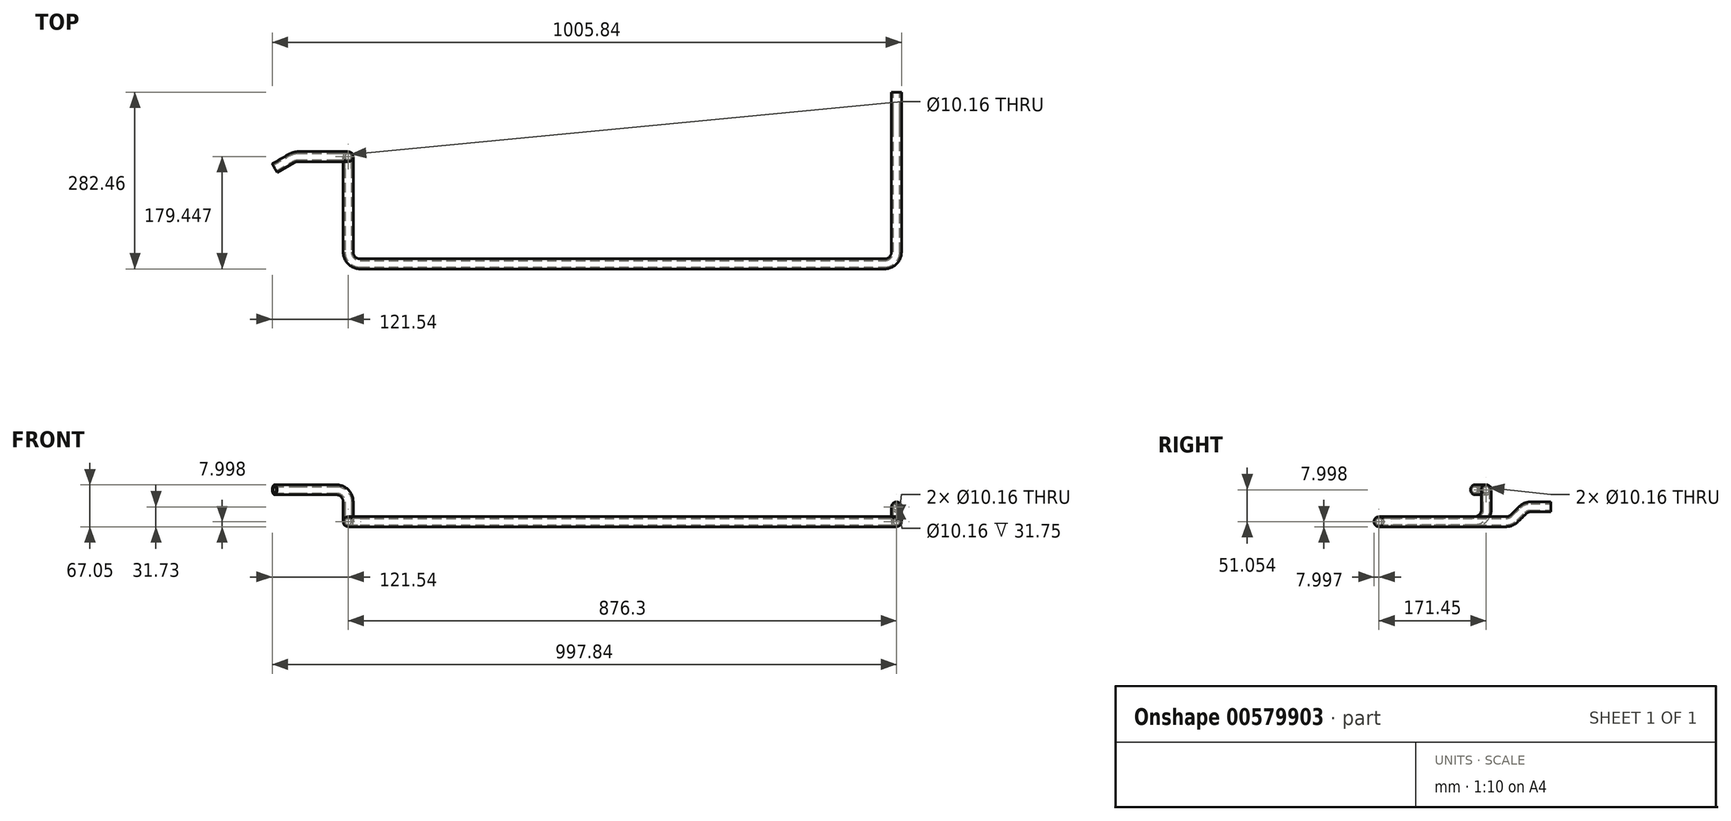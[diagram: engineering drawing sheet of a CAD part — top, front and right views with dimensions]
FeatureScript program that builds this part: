
annotation { "Feature Type Name" : "Feature", "Feature Type Description" : "" }
export const myFeature = defineFeature(function(context is Context, id is Id, definition is map)
    precondition{}
    {
        {
            var Q0;
            Q0=qCreatedBy(makeId("Front.planeOp"),FACE);
            var sketch = newSketch(context, id + "F0", { "sketchPlane" : qUnion([Q0])});
            skCircle(sketch, "E0", {"center": v(0, 0) * mm, "radius": 8 * mm});
            skCircle(sketch, "E1", {"center": v(0, 0) * mm, "radius": 5.08 * mm});
            skSolve(sketch);
        }
        {
            var Q0;
            Q0=qSketchRegion(id+"F0",true);
            extrude(context, id + "F1", {"entities" : qUnion([Q0]), "depth" : 31.75 * mm, "offsetDistance" : 25.4 * mm});
        }
        {
            var Q0;
            Q0=makeQuery(id+"F1.opExtrude","CAP_FACE",FACE,{"disambiguationData":[OSD([sQuery(id+"F0.wireOp",EDGE,"E0"),sQuery(id+"F0.wireOp",EDGE,"E1")])],"isStart":false});
            var sketch = newSketch(context, id + "F2", { "sketchPlane" : qUnion([Q0])});
            skCircle(sketch, "E2", {"center": v(0, 0) * mm, "radius": 5.08 * mm});
            skCircle(sketch, "E3", {"center": v(0, 0) * mm, "radius": 8 * mm});
            skLineSegment(sketch, "E4", {"start": v(-12.88, -19.05) * mm, "end": v(12.35, -19.05) * mm});
            skSolve(sketch);
        }
        {
            var Q0;
            Q0 = qSketchRegion(id + "F2", true);
            var Q1;
            Q1=sQuery(id+"F2.wireOp",EDGE,"E4");
            revolve(context, id + "F3", {"operationType" : NewBodyOperationType.ADD, "entities" : qUnion([Q0]), "axis" : qUnion([Q1]), "revolveType" : RevolveType.ONE_DIRECTION, "angle" : 45 * degree});
        }
        {
            var Q0;
            Q0=makeQuery(id+"F3.opRevolve","CAP_FACE",FACE,{"disambiguationData":[OSD([sQuery(id+"F2.wireOp",EDGE,"E2"),sQuery(id+"F2.wireOp",EDGE,"E3")])],"isStart":false});
            var sketch = newSketch(context, id + "F4", { "sketchPlane" : qUnion([Q0])});
            skCircle(sketch, "E5", {"center": v(0, 28.03) * mm, "radius": 5.08 * mm});
            skCircle(sketch, "E6", {"center": v(0, 28.03) * mm, "radius": 8 * mm});
            skSolve(sketch);
        }
        {
            var Q0;
            Q0 = qSketchRegion(id + "F4", true);
            extrude(context, id + "F5", {"entities" : qUnion([Q0]), "operationType" : NewBodyOperationType.ADD, "depth" : 17.78 * mm, "offsetDistance" : 25.4 * mm});
        }
        {
            var Q0;
            Q0=makeQuery(id+"F5.opExtrude","CAP_FACE",FACE,{"disambiguationData":[OSD([sQuery(id+"F4.wireOp",EDGE,"E5"),sQuery(id+"F4.wireOp",EDGE,"E6")])],"isStart":false});
            var sketch = newSketch(context, id + "F6", { "sketchPlane" : qUnion([Q0])});
            skCircle(sketch, "E7", {"center": v(0, 28.03) * mm, "radius": 5.08 * mm});
            skCircle(sketch, "E8", {"center": v(0, 28.03) * mm, "radius": 8 * mm});
            skLineSegment(sketch, "E9", {"start": v(-8.48, 47.08) * mm, "end": v(8.76, 47.08) * mm});
            skSolve(sketch);
        }
        {
            var Q0;
            Q0 = qSketchRegion(id + "F6", true);
            var Q1;
            Q1=sQuery(id+"F6.wireOp",EDGE,"E9");
            revolve(context, id + "F7", {"operationType" : NewBodyOperationType.ADD, "entities" : qUnion([Q0]), "axis" : qUnion([Q1]), "revolveType" : RevolveType.ONE_DIRECTION, "oppositeDirection" : true, "angle" : 45 * degree});
        }
        {
            var Q0;
            Q0=makeQuery(id+"F7.opRevolve","CAP_FACE",FACE,{"disambiguationData":[OSD([sQuery(id+"F6.wireOp",EDGE,"E7"),sQuery(id+"F6.wireOp",EDGE,"E8")])],"isStart":false});
            var sketch = newSketch(context, id + "F8", { "sketchPlane" : qUnion([Q0])});
            skCircle(sketch, "E10", {"center": v(0, -23.73) * mm, "radius": 5.08 * mm});
            skCircle(sketch, "E11", {"center": v(0, -23.73) * mm, "radius": 8 * mm});
            skSolve(sketch);
        }
        {
            var Q0;
            Q0 = qSketchRegion(id + "F8", true);
            extrude(context, id + "F9", {"entities" : qUnion([Q0]), "operationType" : NewBodyOperationType.ADD, "depth" : 184.15 * mm, "offsetDistance" : 25.4 * mm});
        }
        {
            var Q0;
            Q0=makeQuery(id+"F9.opExtrude","CAP_FACE",FACE,{"disambiguationData":[OSD([sQuery(id+"F8.wireOp",EDGE,"E10"),sQuery(id+"F8.wireOp",EDGE,"E11")])],"isStart":false});
            var sketch = newSketch(context, id + "F10", { "sketchPlane" : qUnion([Q0])});
            skCircle(sketch, "E12", {"center": v(0, -23.73) * mm, "radius": 5.08 * mm});
            skCircle(sketch, "E13", {"center": v(0, -23.73) * mm, "radius": 8 * mm});
            skLineSegment(sketch, "E14", {"start": v(-19.05, -18.56) * mm, "end": v(-19.05, -27.46) * mm});
            skSolve(sketch);
        }
        {
            var Q0;
            Q0 = qSketchRegion(id + "F10", true);
            var Q1;
            Q1=sQuery(id+"F10.wireOp",EDGE,"E14");
            revolve(context, id + "F11", {"operationType" : NewBodyOperationType.ADD, "entities" : qUnion([Q0]), "axis" : qUnion([Q1]), "revolveType" : RevolveType.ONE_DIRECTION, "angle" : 90 * degree});
        }
        {
            var Q0;
            Q0=makeQuery(id+"F11.opRevolve","CAP_FACE",FACE,{"disambiguationData":[OSD([sQuery(id+"F10.wireOp",EDGE,"E12"),sQuery(id+"F10.wireOp",EDGE,"E13")])],"isStart":false});
            var sketch = newSketch(context, id + "F12", { "sketchPlane" : qUnion([Q0])});
            skCircle(sketch, "E15", {"center": v(274.46, -23.73) * mm, "radius": 5.08 * mm});
            skCircle(sketch, "E16", {"center": v(274.46, -23.73) * mm, "radius": 8 * mm});
            skSolve(sketch);
        }
        {
            var Q0;
            Q0 = qSketchRegion(id + "F12", true);
            extrude(context, id + "F13", {"entities" : qUnion([Q0]), "operationType" : NewBodyOperationType.ADD, "depth" : 838.2 * mm, "offsetDistance" : 25.4 * mm});
        }
        {
            var Q0;
            Q0=makeQuery(id+"F13.opExtrude","CAP_FACE",FACE,{"disambiguationData":[OSD([sQuery(id+"F12.wireOp",EDGE,"E15"),sQuery(id+"F12.wireOp",EDGE,"E16")])],"isStart":false});
            var sketch = newSketch(context, id + "F14", { "sketchPlane" : qUnion([Q0])});
            skCircle(sketch, "E17", {"center": v(274.46, -23.73) * mm, "radius": 5.08 * mm});
            skCircle(sketch, "E18", {"center": v(274.46, -23.73) * mm, "radius": 8 * mm});
            skLineSegment(sketch, "E19", {"start": v(255.41, -17.25) * mm, "end": v(255.41, -29.27) * mm});
            skSolve(sketch);
        }
        {
            var Q0;
            Q0 = qSketchRegion(id + "F14", true);
            var Q1;
            Q1=sQuery(id+"F14.wireOp",EDGE,"E19");
            revolve(context, id + "F15", {"operationType" : NewBodyOperationType.ADD, "entities" : qUnion([Q0]), "axis" : qUnion([Q1]), "revolveType" : RevolveType.ONE_DIRECTION, "angle" : 90 * degree});
        }
        {
            var Q0;
            Q0=makeQuery(id+"F15.opRevolve","CAP_FACE",FACE,{"disambiguationData":[OSD([sQuery(id+"F14.wireOp",EDGE,"E17"),sQuery(id+"F14.wireOp",EDGE,"E18")])],"isStart":false});
            var sketch = newSketch(context, id + "F16", { "sketchPlane" : qUnion([Q0])});
            skCircle(sketch, "E20", {"center": v(876.3, -23.73) * mm, "radius": 5.08 * mm});
            skCircle(sketch, "E21", {"center": v(876.3, -23.73) * mm, "radius": 8 * mm});
            skSolve(sketch);
        }
        {
            var Q0;
            Q0 = qSketchRegion(id + "F16", true);
            extrude(context, id + "F17", {"entities" : qUnion([Q0]), "operationType" : NewBodyOperationType.ADD, "depth" : 133.35 * mm, "offsetDistance" : 25.4 * mm});
        }
        {
            var Q0;
            Q0=makeQuery(id+"F17.opExtrude","CAP_FACE",FACE,{"disambiguationData":[OSD([sQuery(id+"F16.wireOp",EDGE,"E20"),sQuery(id+"F16.wireOp",EDGE,"E21")])],"isStart":false});
            var sketch = newSketch(context, id + "F18", { "sketchPlane" : qUnion([Q0])});
            skCircle(sketch, "E22", {"center": v(876.3, -23.73) * mm, "radius": 5.08 * mm});
            skCircle(sketch, "E23", {"center": v(876.3, -23.73) * mm, "radius": 8 * mm});
            skLineSegment(sketch, "E24", {"start": v(865.65, -4.68) * mm, "end": v(887.31, -4.68) * mm});
            skSolve(sketch);
        }
        {
            var Q0;
            Q0 = qSketchRegion(id + "F18", true);
            var Q1;
            Q1=sQuery(id+"F18.wireOp",EDGE,"E24");
            revolve(context, id + "F19", {"operationType" : NewBodyOperationType.ADD, "entities" : qUnion([Q0]), "axis" : qUnion([Q1]), "revolveType" : RevolveType.ONE_DIRECTION, "oppositeDirection" : true, "angle" : 90 * degree});
        }
        {
            var Q0;
            Q0=makeQuery(id+"F19.opRevolve","CAP_FACE",FACE,{"disambiguationData":[OSD([sQuery(id+"F18.wireOp",EDGE,"E22"),sQuery(id+"F18.wireOp",EDGE,"E23")])],"isStart":false});
            var sketch = newSketch(context, id + "F20", { "sketchPlane" : qUnion([Q0])});
            skCircle(sketch, "E25", {"center": v(-876.3, -103.01) * mm, "radius": 5.08 * mm});
            skCircle(sketch, "E26", {"center": v(-876.3, -103.01) * mm, "radius": 8 * mm});
            skSolve(sketch);
        }
        {
            var Q0;
            Q0 = qSketchRegion(id + "F20", true);
            extrude(context, id + "F21", {"entities" : qUnion([Q0]), "operationType" : NewBodyOperationType.ADD, "depth" : 12.95 * mm, "offsetDistance" : 25.4 * mm});
        }
        {
            var Q0;
            Q0=makeQuery(id+"F21.opExtrude","CAP_FACE",FACE,{"disambiguationData":[OSD([sQuery(id+"F20.wireOp",EDGE,"E25"),sQuery(id+"F20.wireOp",EDGE,"E26")])],"isStart":false});
            var sketch = newSketch(context, id + "F22", { "sketchPlane" : qUnion([Q0])});
            skCircle(sketch, "E27", {"center": v(-876.3, -103.01) * mm, "radius": 5.08 * mm});
            skCircle(sketch, "E28", {"center": v(-876.3, -103.01) * mm, "radius": 8 * mm});
            skLineSegment(sketch, "E29", {"start": v(-895.35, -108.5) * mm, "end": v(-895.35, -98.53) * mm});
            skSolve(sketch);
        }
        {
            var Q0;
            Q0 = qSketchRegion(id + "F22", true);
            var Q1;
            Q1=sQuery(id+"F22.wireOp",EDGE,"E29");
            revolve(context, id + "F23", {"operationType" : NewBodyOperationType.ADD, "entities" : qUnion([Q0]), "axis" : qUnion([Q1]), "revolveType" : RevolveType.ONE_DIRECTION, "oppositeDirection" : true, "angle" : 90 * degree});
        }
        {
            var Q0;
            Q0=makeQuery(id+"F23.opRevolve","CAP_FACE",FACE,{"disambiguationData":[OSD([sQuery(id+"F22.wireOp",EDGE,"E27"),sQuery(id+"F22.wireOp",EDGE,"E28")])],"isStart":false});
            var sketch = newSketch(context, id + "F24", { "sketchPlane" : qUnion([Q0])});
            skCircle(sketch, "E30", {"center": v(103.01, 27.32) * mm, "radius": 5.08 * mm});
            skCircle(sketch, "E31", {"center": v(103.01, 27.32) * mm, "radius": 8 * mm});
            skSolve(sketch);
        }
        {
            var Q0;
            Q0 = qSketchRegion(id + "F24", true);
            extrude(context, id + "F25", {"entities" : qUnion([Q0]), "operationType" : NewBodyOperationType.ADD, "depth" : 61.47 * mm, "offsetDistance" : 25.4 * mm});
        }
        {
            var Q0;
            Q0=makeQuery(id+"F25.opExtrude","CAP_FACE",FACE,{"disambiguationData":[OSD([sQuery(id+"F24.wireOp",EDGE,"E30"),sQuery(id+"F24.wireOp",EDGE,"E31")])],"isStart":false});
            var sketch = newSketch(context, id + "F26", { "sketchPlane" : qUnion([Q0])});
            skCircle(sketch, "E32", {"center": v(103.01, 27.32) * mm, "radius": 5.08 * mm});
            skCircle(sketch, "E33", {"center": v(103.01, 27.32) * mm, "radius": 8 * mm});
            skLineSegment(sketch, "E34", {"start": v(122.06, 35.13) * mm, "end": v(122.06, 17.42) * mm});
            skSolve(sketch);
        }
        {
            var Q0;
            Q0 = qSketchRegion(id + "F26", true);
            var Q1;
            Q1=sQuery(id+"F26.wireOp",EDGE,"E34");
            revolve(context, id + "F27", {"operationType" : NewBodyOperationType.ADD, "entities" : qUnion([Q0]), "axis" : qUnion([Q1]), "revolveType" : RevolveType.ONE_DIRECTION, "oppositeDirection" : true, "angle" : 30 * degree});
        }
        {
            var Q0;
            Q0=makeQuery(id+"F27.opRevolve","CAP_FACE",FACE,{"disambiguationData":[OSD([sQuery(id+"F26.wireOp",EDGE,"E32"),sQuery(id+"F26.wireOp",EDGE,"E33")])],"isStart":false});
            var sketch = newSketch(context, id + "F28", { "sketchPlane" : qUnion([Q0])});
            skCircle(sketch, "E35", {"center": v(-391.75, 27.32) * mm, "radius": 5.08 * mm});
            skCircle(sketch, "E36", {"center": v(-391.75, 27.32) * mm, "radius": 8 * mm});
            skSolve(sketch);
        }
        {
            var Q0;
            Q0 = qSketchRegion(id + "F28", true);
            extrude(context, id + "F29", {"entities" : qUnion([Q0]), "operationType" : NewBodyOperationType.ADD, "depth" : 31.75 * mm, "offsetDistance" : 25.4 * mm});
        }
    });
